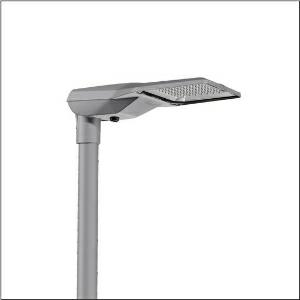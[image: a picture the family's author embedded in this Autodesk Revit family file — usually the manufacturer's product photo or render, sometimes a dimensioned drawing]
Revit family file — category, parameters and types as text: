
# Revit family: streetlight_sl_21_midi___p0_5a_5xe3v33r08nb_a07d
name_source: partatom
category: Lighting Fixtures
units: mm (PartAtom-declared; Revit-internal decimal feet)

## family parameters
Cut with Voids When Loaded = No
Host = Face
Light Source = No
Part Type = Normal
Room Calculation Point = No
Round Connector Dimension = Use Diameter
Shared = No

## types (1)
- --- (1 x LED, 22310 lm, 151.2 W, 3000K)
    Apparent Load = 151 VA
    CIE Flux Codes = 37 73 96 100 100
    Color Rendering = 70
    Color Temperature = 3000K
    Default Elevation = 1800 mm
    Description = Streetlight SL 21 midi, mast luminaire, primary light control with lens, of PMMA, primary optical cover: cover, of toughened safety glass, transparent, light distribution: P0.5a, light emission: direct distribution, primary light characteristic: asymmetric, installation type: post-top, side-entry, LED, High Power LED, rated luminous flux: 22.310lm, luminous efficacy: 148lm/W, light colour: 730, colour temperature: 3000K, control gear: D4i, control: pre-setting: logarithmic dimming characteristic, flexible luminous flux parameterisation, time-dependent luminous flux control, constant luminous flux control, overheat protection, mains connection: 230..240V, AC, 50/60Hz, start of lifetime: 151W, end of service life: 157W, reduction: 70W, luminaire housing, of diecast aluminium, powder-coated, SITECO metallic grey (DB 702S), corrosivity category C5 high according to DIN EN ISO 12944, multi-level sealing system, sealing non-destructively replaceable, inclination adjustable: 0°, 5°, 10°, 15°, please order mast flange separately, length: 644mm, width: 335mm, height: 110mm, mast flange for spigot size: 42mm (side-entry): 5XC10008XM4, 60/48mm (side-entry/post-top): 5XC10108XM2, 76/60mm (side-entry/post-top): 5XC10108XM1, mounting height: 4..8m, Smart Interface below, protection rating (complete): IP66, insulation class (complete): insulation class II (safety insulation), certification: CE, ENEC, ENEC+, VDE, impact resistance: IK10, permissible operating ambient temperature for outdoor applications: -40..+50°C, standard-compliant lighting for roads and squares, packaging unit: 1 piece

Light Distribution: P0.5a
    Height = 111 mm
    Lamp = 1 x LED
    Lamp Light Flux = 22310 lm
    Lamp Power = 151.2 W
    Lamp count = 1
    Length = 644 mm
    Luminous efficacy = 148 lm/W
    Manufacturer = Siteco
    ModVariant = No
    Model = 5XE3V33R08NB
    Number of Poles = 1
    OnlyDefault = Yes
    Power Factor = 1
    Product Name = Streetlight SL 21 midi | P0.5a
    Product group = mast luminaire | pylon top
    ProductGroupID = 6100
    Protection Class = Protection class II
    Protection Degree = IP 66
    RLX_Detail_Level = 1
    RLX_Emergency_Light_Flux = 0 lm
    RLX_Emergency_Type = 0
    RLX_Emergency_Type_DB = No
    RlxData = <blob elided: 90805 chars, md5=fa0446e4>
    Socket = socket
    Standby Power = 0 W
    System Light Flux = 22310 lm
    System Power = 151 W
    Type Comments = factory setting: luminous flux: 100 % | dim-lin: 254 | 802 mA
    Type Image = l_1004300.jpg
    URL = http://relux.com
    VarID = @adj_076821
    Voltage = 0 V
    Weight = 0.00 kg
    Width = 336 mm

## geometry (parser evidence)
native form markers: Blend x4, Sweep x12
no freeform markers — native parametric forms only
